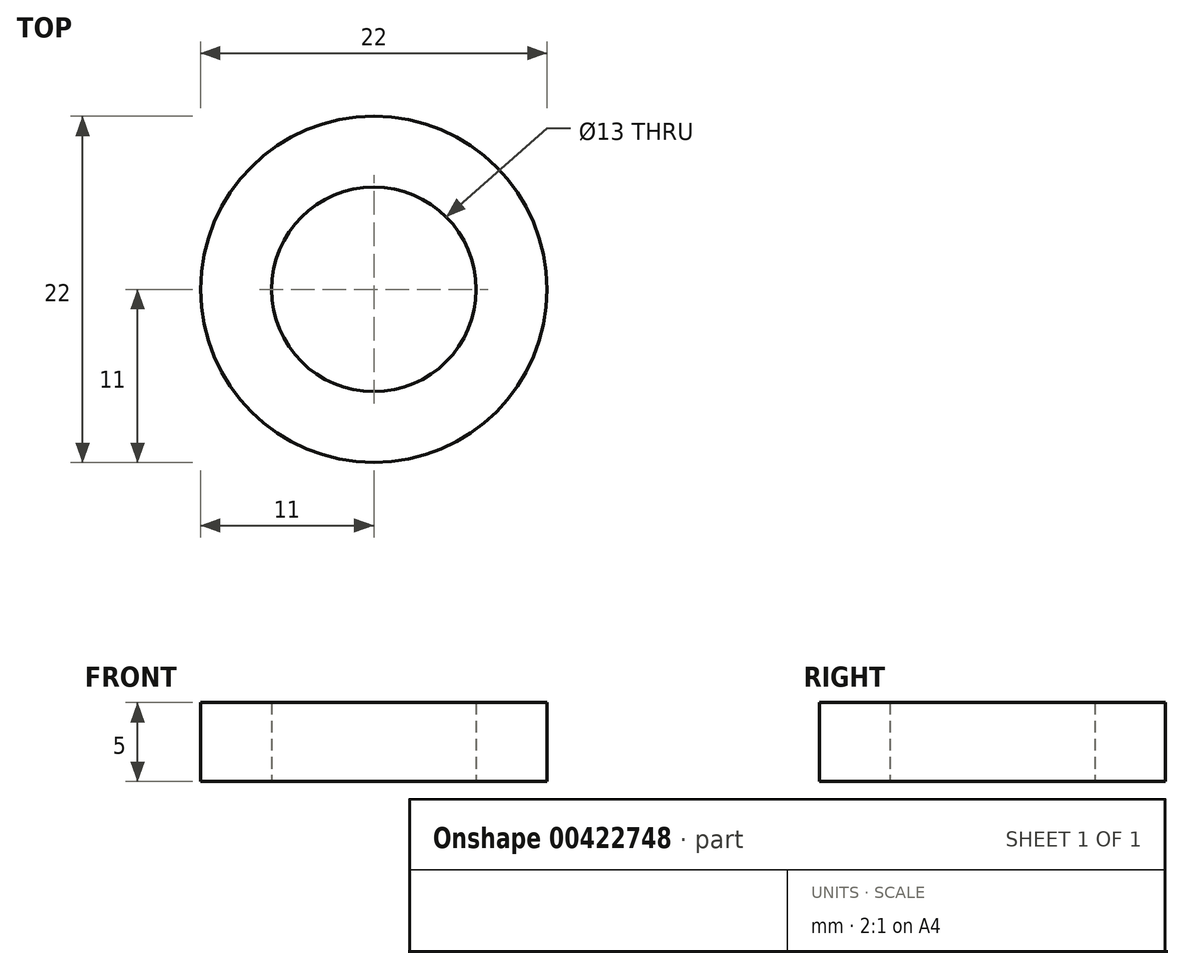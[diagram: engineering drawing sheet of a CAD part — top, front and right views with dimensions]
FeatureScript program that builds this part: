
annotation { "Feature Type Name" : "Feature", "Feature Type Description" : "" }
export const myFeature = defineFeature(function(context is Context, id is Id, definition is map)
    precondition{}
    {
        {
            var Q0;
            Q0=qCreatedBy(makeId("Top.planeOp"),FACE);
            var sketch = newSketch(context, id + "F0", { "sketchPlane" : qUnion([Q0])});
            skCircle(sketch, "E0", {"center": v(0, 0) * mm, "radius": 11 * mm});
            skCircle(sketch, "E1", {"center": v(0, 0) * mm, "radius": 6.5 * mm});
            skSolve(sketch);
        }
        {
            var Q0;
            Q0=makeQuery(id+"F0.imprint","IMPRINT",FACE,{"disambiguationData":[TD([[makeQuery(id+"F0.imprint","IMPRINT",EDGE,{"derivedFrom":sQuery(id+"F0.wireOp",EDGE,"E0")}),1.0]])]});
            extrude(context, id + "F1", {"entities" : qUnion([Q0]), "depth" : 5 * mm});
        }
    });
